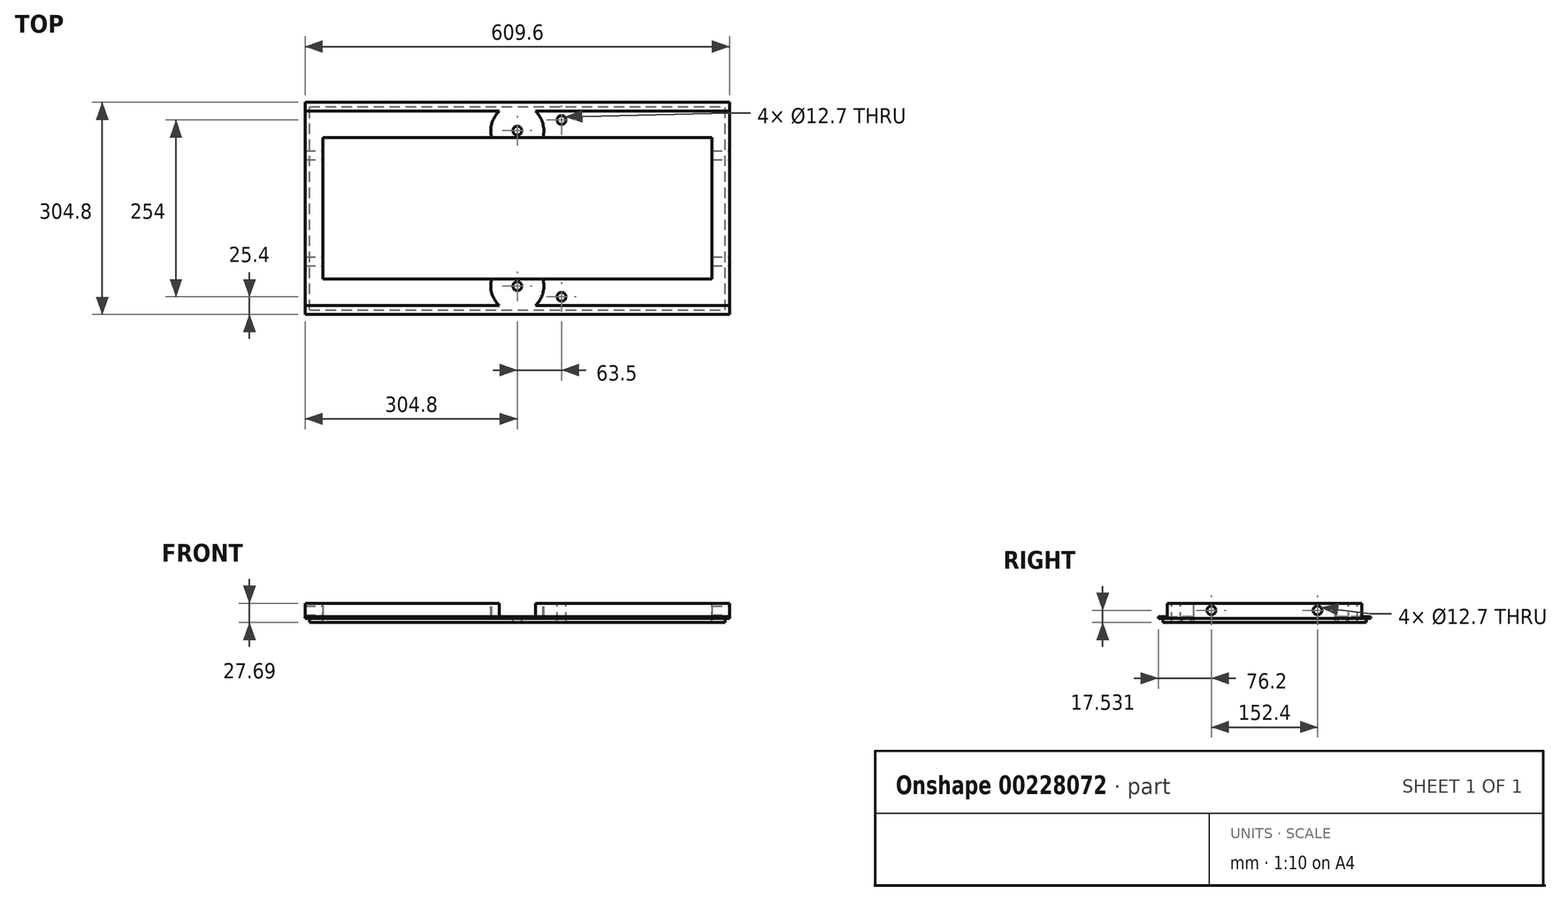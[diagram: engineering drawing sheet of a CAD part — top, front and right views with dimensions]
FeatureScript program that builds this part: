
annotation { "Feature Type Name" : "Feature", "Feature Type Description" : "" }
export const myFeature = defineFeature(function(context is Context, id is Id, definition is map)
    precondition{}
    {
        {
            var Q0;
            Q0=qCreatedBy(makeId("Top.planeOp"),FACE);
            var sketch = newSketch(context, id + "F0", { "sketchPlane" : qUnion([Q0])});
            skLineSegment(sketch, "E0.bottom", {"start": v(0, 0) * mm, "end": v(609.6, 0) * mm});
            skLineSegment(sketch, "E0.top", {"start": v(0, 304.8) * mm, "end": v(609.6, 304.8) * mm});
            skLineSegment(sketch, "E0.left", {"start": v(0, 0) * mm, "end": v(0, 304.8) * mm});
            skLineSegment(sketch, "E0.right", {"start": v(609.6, 0) * mm, "end": v(609.6, 304.8) * mm});
            skSolve(sketch);
        }
        {
            var Q0;
            Q0=qSketchRegion(id+"F0",true);
            extrude(context, id + "F1", {"entities" : qUnion([Q0]), "depth" : 21.97 * mm});
        }
        {
            var Q0;
            Q0=makeQuery(id+"F1.opExtrude","CAP_FACE",FACE,{"disambiguationData":[OSD([sQuery(id+"F0.wireOp",EDGE,"E0.bottom"),sQuery(id+"F0.wireOp",EDGE,"E0.top"),sQuery(id+"F0.wireOp",EDGE,"E0.left"),sQuery(id+"F0.wireOp",EDGE,"E0.right")])],"isStart":true});
            var sketch = newSketch(context, id + "F2", { "sketchPlane" : qUnion([Q0])});
            skLineSegment(sketch, "E1.bottom", {"start": v(6.35, -6.35) * mm, "end": v(603.25, -6.35) * mm});
            skLineSegment(sketch, "E1.top", {"start": v(6.35, -298.45) * mm, "end": v(603.25, -298.45) * mm});
            skLineSegment(sketch, "E1.left", {"start": v(6.35, -6.35) * mm, "end": v(6.35, -298.45) * mm});
            skLineSegment(sketch, "E1.right", {"start": v(603.25, -6.35) * mm, "end": v(603.25, -298.45) * mm});
            skSolve(sketch);
        }
        {
            var Q0;
            Q0=qSketchRegion(id+"F2",true);
            extrude(context, id + "F3", {"entities" : qUnion([Q0]), "operationType" : NewBodyOperationType.ADD, "depth" : 5.7 * mm});
        }
        {
            var Q0;
            Q0=makeQuery(id+"F1.opExtrude","CAP_FACE",FACE,{"disambiguationData":[OSD([sQuery(id+"F0.wireOp",EDGE,"E0.bottom"),sQuery(id+"F0.wireOp",EDGE,"E0.top"),sQuery(id+"F0.wireOp",EDGE,"E0.left"),sQuery(id+"F0.wireOp",EDGE,"E0.right")])],"isStart":false});
            var sketch = newSketch(context, id + "F4", { "sketchPlane" : qUnion([Q0])});
            skLineSegment(sketch, "E2.bottom", {"start": v(94.92, 87.47) * mm, "end": v(349.59, 87.47) * mm});
            skLineSegment(sketch, "E2.top", {"start": v(94.92, 220.47) * mm, "end": v(349.59, 220.47) * mm});
            skLineSegment(sketch, "E2.left", {"start": v(94.92, 87.47) * mm, "end": v(94.92, 220.47) * mm});
            skLineSegment(sketch, "E2.right", {"start": v(349.59, 87.47) * mm, "end": v(349.59, 220.47) * mm});
            skSolve(sketch);
        }
        {
            var Q0;
            Q0=makeQuery(id+"F4.imprint","IMPRINT",FACE,{"disambiguationData":[TD([[makeQuery(id+"F4.imprint","IMPRINT",EDGE,{"derivedFrom":sQuery(id+"F4.wireOp",EDGE,"E2.bottom")}),-1.0]])]});
            var sketch = newSketch(context, id + "F5", { "sketchPlane" : qUnion([Q0])});
            skLineSegment(sketch, "E3.bottom", {"start": v(25.4, 254) * mm, "end": v(584.2, 254) * mm});
            skLineSegment(sketch, "E3.top", {"start": v(25.4, 50.8) * mm, "end": v(584.2, 50.8) * mm});
            skLineSegment(sketch, "E3.left", {"start": v(25.4, 254) * mm, "end": v(25.4, 50.8) * mm});
            skLineSegment(sketch, "E3.right", {"start": v(584.2, 254) * mm, "end": v(584.2, 50.8) * mm});
            skSolve(sketch);
        }
        {
            var Q0;
            Q0=qSketchRegion(id+"F5",true);
            extrude(context, id + "F6", {"entities" : qUnion([Q0]), "operationType" : NewBodyOperationType.REMOVE, "endBound" : BoundingType.THROUGH_ALL, "oppositeDirection" : true, "depth" : 25.4 * mm});
        }
        {
            var Q0;
            Q0=makeQuery(id+"F4.imprint","IMPRINT",FACE,{"disambiguationData":[TD([[makeQuery(id+"F4.imprint","IMPRINT",EDGE,{"derivedFrom":sQuery(id+"F4.wireOp",EDGE,"E2.bottom")}),-1.0]])]});
            var sketch = newSketch(context, id + "F7", { "sketchPlane" : qUnion([Q0])});
            skSolve(sketch);
        }
        {
            var Q0;
            Q0=makeQuery(id+"F1.opExtrude","SWEPT_FACE",FACE,{"disambiguationData":[OSD([sQuery(id+"F0.wireOp",EDGE,"E0.left")])]});
            var sketch = newSketch(context, id + "F8", { "sketchPlane" : qUnion([Q0])});
            skLineSegment(sketch, "E4.bottom", {"start": v(-304.8, 21.97) * mm, "end": v(-292.1, 21.97) * mm});
            skLineSegment(sketch, "E4.top", {"start": v(-304.8, 2.54) * mm, "end": v(-292.1, 2.54) * mm});
            skLineSegment(sketch, "E4.left", {"start": v(-304.8, 21.97) * mm, "end": v(-304.8, 2.54) * mm});
            skLineSegment(sketch, "E4.right", {"start": v(-292.1, 21.97) * mm, "end": v(-292.1, 2.54) * mm});
            skLineSegment(sketch, "E5.bottom", {"start": v(0, 21.97) * mm, "end": v(-12.7, 21.97) * mm});
            skLineSegment(sketch, "E5.top", {"start": v(0, 2.54) * mm, "end": v(-12.7, 2.54) * mm});
            skLineSegment(sketch, "E5.left", {"start": v(0, 21.97) * mm, "end": v(0, 2.54) * mm});
            skLineSegment(sketch, "E5.right", {"start": v(-12.7, 21.97) * mm, "end": v(-12.7, 2.54) * mm});
            skSolve(sketch);
        }
        {
            var Q0;
            Q0 = qSketchRegion(id + "F8", true);
            extrude(context, id + "F9", {"entities" : qUnion([Q0]), "operationType" : NewBodyOperationType.REMOVE, "endBound" : BoundingType.THROUGH_ALL, "oppositeDirection" : true, "depth" : 25.4 * mm, "offsetDistance" : 25.4 * mm});
        }
        {
            var Q0;
            Q0=makeQuery(id+"F7.imprint","IMPRINT",FACE,{"disambiguationData":[TD([[makeQuery(id+"F7.imprint","IMPRINT",EDGE,{"derivedFrom":makeQuery(id+"F4.imprint","IMPRINT",EDGE,{"derivedFrom":sQuery(id+"F4.wireOp",EDGE,"E2.bottom")})}),-1.0]])]});
            var sketch = newSketch(context, id + "F10", { "sketchPlane" : qUnion([Q0])});
            skCircle(sketch, "E6", {"center": v(304.8, 40.64) * mm, "radius": 38.1 * mm});
            skLineSegment(sketch, "E7", {"start": v(0, 40.64) * mm, "end": v(609.6, 40.64) * mm, "construction": true});
            skLineSegment(sketch, "E8", {"start": v(0, 264.16) * mm, "end": v(609.6, 264.16) * mm, "construction": true});
            skPoint(sketch, "E9.startSnap0", {"position": v(304.8, 264.16) * mm});
            skCircle(sketch, "E10", {"center": v(304.8, 264.16) * mm, "radius": 38.1 * mm});
            skSolve(sketch);
        }
        {
            var Q0;
            Q0 = qSketchRegion(id + "F10", true);
            var Q1;
            Q1=makeQuery(id+"F9.boolean.opBoolean","COPY",FACE,{"derivedFrom":makeQuery(id+"F9.opExtrude","SWEPT_FACE",FACE,{"disambiguationData":[OSD([sQuery(id+"F8.wireOp",EDGE,"E5.top")])]})});
            extrude(context, id + "F11", {"entities" : qUnion([Q0]), "operationType" : NewBodyOperationType.REMOVE, "endBound" : BoundingType.UP_TO_SURFACE, "oppositeDirection" : true, "depth" : 25.4 * mm, "endBoundEntityFace" : qUnion([Q1]), "offsetDistance" : 25.4 * mm});
        }
        {
            var Q0;
            Q0=makeQuery(id+"F11.boolean.opBoolean","MERGE",FACE,{"derivedFrom":[makeQuery(id+"F9.boolean.opBoolean","COPY",FACE,{"derivedFrom":makeQuery(id+"F9.opExtrude","SWEPT_FACE",FACE,{"disambiguationData":[OSD([sQuery(id+"F8.wireOp",EDGE,"E4.top")])]})}),makeQuery(id+"F11.opExtrude","CAP_FACE",FACE,{"disambiguationData":[OSD([sQuery(id+"F8.wireOp",EDGE,"E5.top")]),OD(1.0)],"isStart":false})]});
            var sketch = newSketch(context, id + "F12", { "sketchPlane" : qUnion([Q0])});
            skCircle(sketch, "E11", {"center": v(304.8, 264.16) * mm, "radius": 6.35 * mm});
            skCircle(sketch, "E12", {"center": v(304.8, 40.64) * mm, "radius": 6.35 * mm});
            skSolve(sketch);
        }
        {
            var Q0;
            Q0 = qSketchRegion(id + "F12", true);
            extrude(context, id + "F13", {"entities" : qUnion([Q0]), "operationType" : NewBodyOperationType.REMOVE, "endBound" : BoundingType.THROUGH_ALL, "oppositeDirection" : true, "depth" : 25.4 * mm, "offsetDistance" : 25.4 * mm});
        }
        {
            var Q0;
            Q0=makeQuery(id+"F1.opExtrude","SWEPT_FACE",FACE,{"disambiguationData":[OSD([sQuery(id+"F0.wireOp",EDGE,"E0.right")])]});
            var sketch = newSketch(context, id + "F14", { "sketchPlane" : qUnion([Q0])});
            skCircle(sketch, "E13", {"center": v(228.6, 11.81) * mm, "radius": 6.35 * mm});
            skCircle(sketch, "E14", {"center": v(76.2, 11.81) * mm, "radius": 6.35 * mm});
            skSolve(sketch);
        }
        {
            var Q0;
            Q0 = qSketchRegion(id + "F14", true);
            extrude(context, id + "F15", {"entities" : qUnion([Q0]), "operationType" : NewBodyOperationType.REMOVE, "endBound" : BoundingType.THROUGH_ALL, "oppositeDirection" : true, "depth" : 25.4 * mm, "offsetDistance" : 25.4 * mm});
        }
        {
            var Q0;
            {var subQ0=sQuery(id+"F0.wireOp",EDGE,"E0.right");Q0=makeQuery(id+"F11.boolean.opBoolean","SPLIT",FACE,{"disambiguationData":[TD([makeQuery(id+"F1.opExtrude","SWEPT_FACE",FACE,{"disambiguationData":[OSD([subQ0])]})])],"derivedFrom":makeQuery(id+"F1.opExtrude","CAP_FACE",FACE,{"disambiguationData":[OSD([sQuery(id+"F0.wireOp",EDGE,"E0.bottom"),sQuery(id+"F0.wireOp",EDGE,"E0.top"),sQuery(id+"F0.wireOp",EDGE,"E0.left"),subQ0])],"isStart":false})});}
            var sketch = newSketch(context, id + "F16", { "sketchPlane" : qUnion([Q0])});
            skCircle(sketch, "E15", {"center": v(368.3, 25.4) * mm, "radius": 6.35 * mm});
            skLineSegment(sketch, "E16", {"start": v(584.2, 152.4) * mm, "end": v(0, 152.4) * mm, "construction": true});
            skCircle(sketch, "E17.MirrorC", {"center": v(368.3, 279.4) * mm, "radius": 6.35 * mm});
            skSolve(sketch);
        }
        {
            var Q0;
            Q0 = qSketchRegion(id + "F16", true);
            extrude(context, id + "F17", {"entities" : qUnion([Q0]), "operationType" : NewBodyOperationType.REMOVE, "endBound" : BoundingType.THROUGH_ALL, "oppositeDirection" : true, "depth" : 25.4 * mm, "offsetDistance" : 25.4 * mm});
        }
    });
